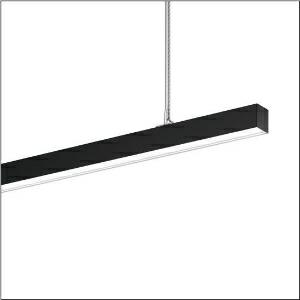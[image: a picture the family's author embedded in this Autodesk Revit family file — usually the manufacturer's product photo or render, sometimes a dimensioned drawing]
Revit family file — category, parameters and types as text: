
# Revit family: silica_r__21_51mx33tat7b_231b
name_source: partatom
category: Lighting Fixtures
units: mm (PartAtom-declared; Revit-internal decimal feet)

## family parameters
Cut with Voids When Loaded = No
Host = Face
Light Source = No
Part Type = Normal
Room Calculation Point = No
Round Connector Dimension = Use Diameter
Shared = No

## types (1)
- --- (1 x LED, 5740 lm, 53.8 W, 6500K)
    Apparent Load = 54 VA
    CIE Flux Codes = 78 96 99 56 100
    Color Rendering = 80
    Color Temperature = 6500K
    Default Elevation = 1800 mm
    Description = Silica® 21, office luminaire, primary optical cover: prismatic diffuser, of PMMA, CAT 2 (L<= 3000cd/m²), light emission: direct/indirect distribution, primary light characteristic: symmetric, installation type: suspended mounting, LED, rated luminous flux: 5.740lm, luminous efficacy: 102lm/W, light colour: 8tw, colour temperature: 2700..6500K, control gear: DALI DT8, with terminal, 3+2-pole, max. 2.5mm², mains connection: 220..240V, AC, 50/60Hz, rated input power: 56.5W, luminaire housing, of aluminium, matt jet black (RAL 9005), length: 1.204mm, width: 53mm, height: 53mm, protection rating (complete): IP20, insulation class (complete): insulation class I (protective earthing), certification: CE, permissible operating ambient temperature: 0..+35°C, standard: EN 50419, packaging unit: 1 piece
    Height = 53 mm
    Lamp = 1 x LED
    Lamp Light Flux = 5740 lm
    Lamp Power = 53.8 W
    Lamp count = 1
    Length = 1204 mm
    Luminous efficacy = 107 lm/W
    Manufacturer = Siteco
    ModVariant = No
    Model = 51MX33TAT7B
    Mounting Place = Ceiling
    Mounting Type = Pendant
    Number of Poles = 1
    OnlyDefault = Yes
    Power Factor = 1
    Product Name = Silica® 21
    Product group = office luminaire | ceiling pendant
    ProductGroupID = 904
    Protection Class = Protection class I
    Protection Degree = IP 20
    RLX_Detail_Level = 1
    RLX_Emergency_Light_Flux = 0 lm
    RLX_Emergency_Type = 0
    RLX_Emergency_Type_DB = No
    RlxData = <blob elided: 22905 chars, md5=8cc4f1ea>
    Socket = socket
    Standby Power = 0 W
    System Light Flux = 5740 lm
    System Power = 54 W
    Type Comments = individual setting
    Type Image = l_1335856.jpg
    URL = http://relux.com
    VarID = @adj_139764
    Voltage = 0 V
    Weight = 0.00 kg
    Width = 53 mm

## geometry (parser evidence)
native form markers: Blend x4, Sweep x14
no freeform markers — native parametric forms only
